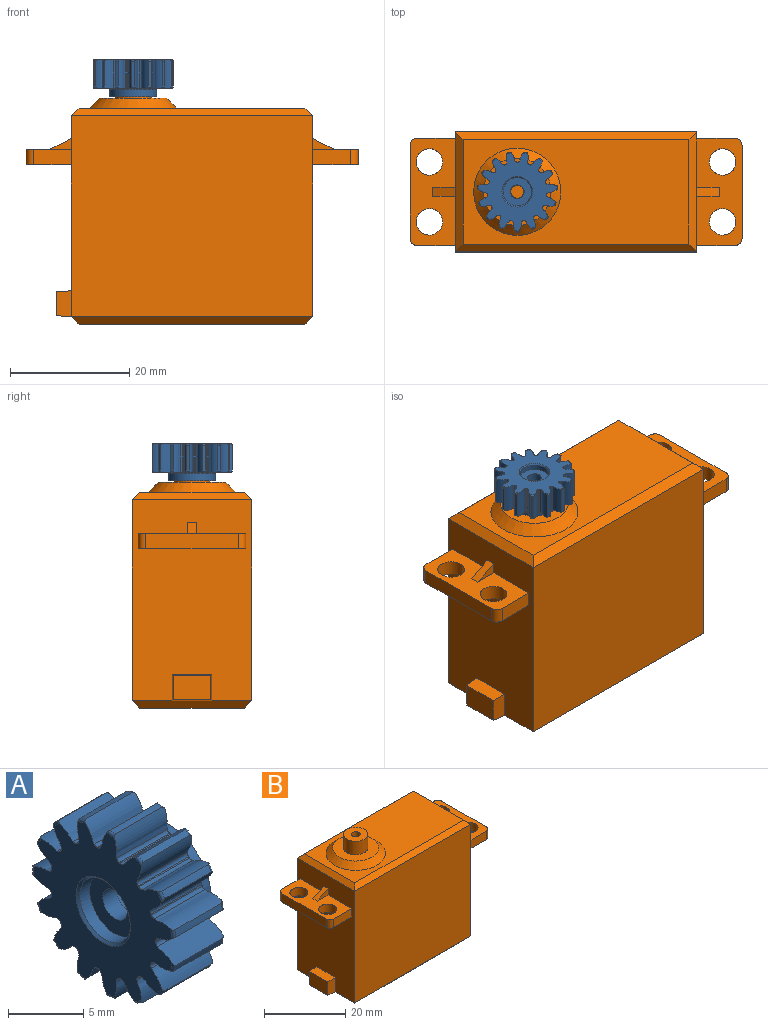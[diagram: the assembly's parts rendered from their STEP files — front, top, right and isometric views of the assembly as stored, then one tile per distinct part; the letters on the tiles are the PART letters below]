
ASSEMBLY  parts=2 mates=1
PART A: 131 faces, bbox 6.2x13.4x13.5 mm
  f0: cylinder r=2.38mm len=4.76mm, axis (-1,0,0), area 13.9mm2, adj f125,f130
  f1: cylinder r=3.96mm len=7.92mm, axis (1,0,0), area 31.3mm2, adj f124,f126
  f2: plane 13.08x13.02mm, normal (-1,0,0), area 86.7mm2, adj f3,f4,f5,f6,f7,f8,f9,f10
  f3: torus R=6.55mm, axis (-1,0,0), area 0.2mm2, adj f2,f18,f56,f57
  f4: torus R=6.55mm, axis (-1,0,0), area 0.2mm2, adj f2,f59,f60,f61
  f5: torus R=6.55mm, axis (-1,0,0), area 0.2mm2, adj f2,f64,f65,f66
  f6: torus R=6.55mm, axis (-1,0,0), area 0.2mm2, adj f2,f69,f70,f71
  f7: torus R=6.55mm, axis (-1,0,0), area 0.2mm2, adj f2,f74,f75,f76
  f8: torus R=6.55mm, axis (-1,0,0), area 0.2mm2, adj f2,f79,f80,f81
  f9: torus R=6.55mm, axis (-1,0,0), area 0.2mm2, adj f2,f84,f85,f86
  f10: torus R=6.55mm, axis (-1,0,0), area 0.2mm2, adj f2,f89,f90,f91
  f11: torus R=6.55mm, axis (-1,0,0), area 0.2mm2, adj f2,f36,f37,f38
  f12: torus R=6.55mm, axis (-1,0,0), area 0.2mm2, adj f2,f94,f95,f96
  f13: torus R=6.55mm, axis (-1,0,0), area 0.2mm2, adj f2,f99,f100,f101
  f14: torus R=6.55mm, axis (-1,0,0), area 0.2mm2, adj f2,f104,f105,f106
  f15: torus R=6.55mm, axis (-1,0,0), area 0.2mm2, adj f2,f109,f110,f111
  f16: torus R=6.55mm, axis (-1,0,0), area 0.2mm2, adj f2,f114,f115,f116
  f17: torus R=6.55mm, axis (-1,0,0), area 0.2mm2, adj f2,f119,f120,f121
  f18: extruded ~4.75x1.34mm, area 8.4mm2, adj f2,f3,f19,f40,f41,f57
  f19: cylinder r=0.31mm len=4.75mm, axis (1,0,0), area 1.6mm2, adj f2,f18,f34,f40
  f20: cylinder r=4.95mm len=4.75mm, axis (1,0,0), area 0.4mm2, adj f2,f35,f40,f92
  f21: cylinder r=4.95mm len=4.75mm, axis (1,0,0), area 0.4mm2, adj f2,f39,f40,f98
  f22: cylinder r=4.95mm len=4.75mm, axis (1,0,0), area 0.4mm2, adj f2,f40,f97,f103
  f23: cylinder r=4.95mm len=4.75mm, axis (1,0,0), area 0.4mm2, adj f2,f40,f102,f108
  f24: cylinder r=4.95mm len=4.75mm, axis (1,0,0), area 0.4mm2, adj f2,f40,f107,f113
  f25: cylinder r=4.95mm len=4.75mm, axis (1,0,0), area 0.4mm2, adj f2,f40,f112,f118
  f26: cylinder r=4.95mm len=4.75mm, axis (1,0,0), area 0.4mm2, adj f2,f40,f117,f123
  f27: cylinder r=4.95mm len=4.75mm, axis (1,0,0), area 0.4mm2, adj f2,f40,f88,f122
  f28: cylinder r=4.95mm len=4.75mm, axis (1,0,0), area 0.4mm2, adj f2,f40,f83,f87
  f29: cylinder r=4.95mm len=4.75mm, axis (1,0,0), area 0.4mm2, adj f2,f40,f78,f82
  f30: cylinder r=4.95mm len=4.75mm, axis (1,0,0), area 0.4mm2, adj f2,f40,f73,f77
  f31: cylinder r=4.95mm len=4.75mm, axis (1,0,0), area 0.4mm2, adj f2,f40,f68,f72
  f32: cylinder r=4.95mm len=4.75mm, axis (1,0,0), area 0.4mm2, adj f2,f40,f63,f67
  f33: cylinder r=4.95mm len=4.75mm, axis (1,0,0), area 0.4mm2, adj f2,f40,f58,f62
  f34: cylinder r=4.95mm len=4.75mm, axis (1,0,0), area 0.4mm2, adj f2,f19,f40,f93
  f35: cylinder r=0.31mm len=4.75mm, axis (1,0,0), area 1.6mm2, adj f2,f20,f36,f40
  f36: extruded ~4.75x1.34mm, area 8.4mm2, adj f2,f11,f35,f37,f40,f49
  f37: cylinder r=6.75mm len=4.35mm, axis (1,0,0), area 2.3mm2, adj f11,f36,f38,f49
  f38: extruded ~4.75x1.73mm, area 8.4mm2, adj f2,f11,f37,f39,f40,f49
  f39: cylinder r=0.31mm len=4.75mm, axis (1,0,0), area 1.6mm2, adj f2,f21,f38,f40
  f40: plane 13.08x13.02mm, normal (1,0,0), area 53.4mm2, adj f18,f19,f20,f21,f22,f23,f24,f25
  f41: torus R=6.55mm, axis (-1,0,0), area 0.2mm2, adj f18,f40,f56,f57
  f42: torus R=6.55mm, axis (-1,0,0), area 0.2mm2, adj f40,f59,f60,f61
  f43: torus R=6.55mm, axis (-1,0,0), area 0.2mm2, adj f40,f64,f65,f66
  f44: torus R=6.55mm, axis (-1,0,0), area 0.2mm2, adj f40,f69,f70,f71
  f45: torus R=6.55mm, axis (-1,0,0), area 0.2mm2, adj f40,f74,f75,f76
  f46: torus R=6.55mm, axis (-1,0,0), area 0.2mm2, adj f40,f79,f80,f81
  f47: torus R=6.55mm, axis (-1,0,0), area 0.2mm2, adj f40,f84,f85,f86
  f48: torus R=6.55mm, axis (-1,0,0), area 0.2mm2, adj f40,f89,f90,f91
  f49: torus R=6.55mm, axis (-1,0,0), area 0.2mm2, adj f36,f37,f38,f40
  f50: torus R=6.55mm, axis (-1,0,0), area 0.2mm2, adj f40,f94,f95,f96
  f51: torus R=6.55mm, axis (-1,0,0), area 0.2mm2, adj f40,f99,f100,f101
  f52: torus R=6.55mm, axis (-1,0,0), area 0.2mm2, adj f40,f104,f105,f106
  f53: torus R=6.55mm, axis (-1,0,0), area 0.2mm2, adj f40,f109,f110,f111
  f54: torus R=6.55mm, axis (-1,0,0), area 0.2mm2, adj f40,f114,f115,f116
  f55: torus R=6.55mm, axis (-1,0,0), area 0.2mm2, adj f40,f119,f120,f121
  f56: extruded ~4.75x1.73mm, area 8.4mm2, adj f2,f3,f40,f41,f57,f58
  f57: cylinder r=6.75mm len=4.35mm, axis (1,0,0), area 2.3mm2, adj f3,f18,f41,f56
  f58: cylinder r=0.31mm len=4.75mm, axis (1,0,0), area 1.6mm2, adj f2,f33,f40,f56
  f59: extruded ~4.75x1.49mm, area 8.4mm2, adj f2,f4,f40,f42,f60,f63
  f60: cylinder r=6.75mm len=4.35mm, axis (1,0,0), area 2.3mm2, adj f4,f42,f59,f61
  f61: extruded ~4.75x1.57mm, area 8.4mm2, adj f2,f4,f40,f42,f60,f62
  f62: cylinder r=0.31mm len=4.75mm, axis (1,0,0), area 1.6mm2, adj f2,f33,f40,f61
  f63: cylinder r=0.31mm len=4.75mm, axis (1,0,0), area 1.6mm2, adj f2,f32,f40,f59
  f64: extruded ~4.75x1.45mm, area 8.4mm2, adj f2,f5,f40,f43,f65,f68
  f65: cylinder r=6.75mm len=4.35mm, axis (1,0,0), area 2.3mm2, adj f5,f43,f64,f66
  f66: extruded ~4.75x1.75mm, area 8.4mm2, adj f2,f5,f40,f43,f65,f67
  f67: cylinder r=0.31mm len=4.75mm, axis (1,0,0), area 1.6mm2, adj f2,f32,f40,f66
  f68: cylinder r=0.31mm len=4.75mm, axis (1,0,0), area 1.6mm2, adj f2,f31,f40,f64
  f69: extruded ~4.75x1.72mm, area 8.4mm2, adj f2,f6,f40,f44,f70,f73
  f70: cylinder r=6.75mm len=4.35mm, axis (1,0,0), area 2.3mm2, adj f6,f44,f69,f71
  f71: extruded ~4.75x1.62mm, area 8.4mm2, adj f2,f6,f40,f44,f70,f72
  f72: cylinder r=0.31mm len=4.75mm, axis (1,0,0), area 1.6mm2, adj f2,f31,f40,f71
  f73: cylinder r=0.31mm len=4.75mm, axis (1,0,0), area 1.6mm2, adj f2,f30,f40,f69
  f74: extruded ~4.75x1.7mm, area 8.4mm2, adj f2,f7,f40,f45,f75,f78
  f75: cylinder r=6.75mm len=4.35mm, axis (1,0,0), area 2.3mm2, adj f7,f45,f74,f76
  f76: extruded ~4.75x1.26mm, area 8.4mm2, adj f2,f7,f40,f45,f75,f77
  f77: cylinder r=0.31mm len=4.75mm, axis (1,0,0), area 1.6mm2, adj f2,f30,f40,f76
  f78: cylinder r=0.31mm len=4.75mm, axis (1,0,0), area 1.6mm2, adj f2,f29,f40,f74
  f79: extruded ~4.75x1.38mm, area 8.4mm2, adj f2,f8,f40,f46,f80,f83
  f80: cylinder r=6.75mm len=4.35mm, axis (1,0,0), area 2.3mm2, adj f8,f46,f79,f81
  f81: extruded ~4.75x1.65mm, area 8.4mm2, adj f2,f8,f40,f46,f80,f82
  f82: cylinder r=0.31mm len=4.75mm, axis (1,0,0), area 1.6mm2, adj f2,f29,f40,f81
  f83: cylinder r=0.31mm len=4.75mm, axis (1,0,0), area 1.6mm2, adj f2,f28,f40,f79
  f84: extruded ~4.75x1.54mm, area 8.4mm2, adj f2,f9,f40,f47,f85,f88
  f85: cylinder r=6.75mm len=4.35mm, axis (1,0,0), area 2.3mm2, adj f9,f47,f84,f86
  f86: extruded ~4.75x1.74mm, area 8.4mm2, adj f2,f9,f40,f47,f85,f87
  f87: cylinder r=0.31mm len=4.75mm, axis (1,0,0), area 1.6mm2, adj f2,f28,f40,f86
  f88: cylinder r=0.31mm len=4.75mm, axis (1,0,0), area 1.6mm2, adj f2,f27,f40,f84
  f89: extruded ~4.75x1.68mm, area 8.4mm2, adj f2,f10,f40,f48,f90,f93
  f90: cylinder r=6.75mm len=4.35mm, axis (1,0,0), area 2.3mm2, adj f10,f48,f89,f91
  f91: extruded ~4.75x1.68mm, area 8.4mm2, adj f2,f10,f40,f48,f90,f92
  f92: cylinder r=0.31mm len=4.75mm, axis (1,0,0), area 1.6mm2, adj f2,f20,f40,f91
  f93: cylinder r=0.31mm len=4.75mm, axis (1,0,0), area 1.6mm2, adj f2,f34,f40,f89
  f94: extruded ~4.75x1.57mm, area 8.4mm2, adj f2,f12,f40,f50,f95,f98
  f95: cylinder r=6.75mm len=4.35mm, axis (1,0,0), area 2.3mm2, adj f12,f50,f94,f96
  f96: extruded ~4.75x1.49mm, area 8.4mm2, adj f2,f12,f40,f50,f95,f97
  f97: cylinder r=0.31mm len=4.75mm, axis (1,0,0), area 1.6mm2, adj f2,f22,f40,f96
  f98: cylinder r=0.31mm len=4.75mm, axis (1,0,0), area 1.6mm2, adj f2,f21,f40,f94
  f99: extruded ~4.75x1.75mm, area 8.4mm2, adj f2,f13,f40,f51,f100,f103
  f100: cylinder r=6.75mm len=4.35mm, axis (1,0,0), area 2.3mm2, adj f13,f51,f99,f101
  f101: extruded ~4.75x1.45mm, area 8.4mm2, adj f2,f13,f40,f51,f100,f102
  f102: cylinder r=0.31mm len=4.75mm, axis (1,0,0), area 1.6mm2, adj f2,f23,f40,f101
  f103: cylinder r=0.31mm len=4.75mm, axis (1,0,0), area 1.6mm2, adj f2,f22,f40,f99
  f104: extruded ~4.75x1.62mm, area 8.4mm2, adj f2,f14,f40,f52,f105,f108
  f105: cylinder r=6.75mm len=4.35mm, axis (1,0,0), area 2.3mm2, adj f14,f52,f104,f106
  f106: extruded ~4.75x1.72mm, area 8.4mm2, adj f2,f14,f40,f52,f105,f107
  f107: cylinder r=0.31mm len=4.75mm, axis (1,0,0), area 1.6mm2, adj f2,f24,f40,f106
  f108: cylinder r=0.31mm len=4.75mm, axis (1,0,0), area 1.6mm2, adj f2,f23,f40,f104
  f109: extruded ~4.75x1.26mm, area 8.4mm2, adj f2,f15,f40,f53,f110,f113
  f110: cylinder r=6.75mm len=4.35mm, axis (1,0,0), area 2.3mm2, adj f15,f53,f109,f111
  f111: extruded ~4.75x1.7mm, area 8.4mm2, adj f2,f15,f40,f53,f110,f112
  f112: cylinder r=0.31mm len=4.75mm, axis (1,0,0), area 1.6mm2, adj f2,f25,f40,f111
  f113: cylinder r=0.31mm len=4.75mm, axis (1,0,0), area 1.6mm2, adj f2,f24,f40,f109
  f114: extruded ~4.75x1.65mm, area 8.4mm2, adj f2,f16,f40,f54,f115,f118
  f115: cylinder r=6.75mm len=4.35mm, axis (1,0,0), area 2.3mm2, adj f16,f54,f114,f116
  f116: extruded ~4.75x1.38mm, area 8.4mm2, adj f2,f16,f40,f54,f115,f117
  f117: cylinder r=0.31mm len=4.75mm, axis (1,0,0), area 1.6mm2, adj f2,f26,f40,f116
  f118: cylinder r=0.31mm len=4.75mm, axis (1,0,0), area 1.6mm2, adj f2,f25,f40,f114
  f119: extruded ~4.75x1.74mm, area 8.4mm2, adj f2,f17,f40,f55,f120,f123
  f120: cylinder r=6.75mm len=4.35mm, axis (1,0,0), area 2.3mm2, adj f17,f55,f119,f121
  f121: extruded ~4.75x1.54mm, area 8.4mm2, adj f2,f17,f40,f55,f120,f122
  f122: cylinder r=0.31mm len=4.75mm, axis (1,0,0), area 1.6mm2, adj f2,f27,f40,f121
  f123: cylinder r=0.31mm len=4.75mm, axis (1,0,0), area 1.6mm2, adj f2,f26,f40,f119
  f124: torus R=4.14mm, axis (1,0,0), area 7.1mm2, adj f1,f40
  f125: cone r=2.47mm half-angle=45deg, axis (-1,0,0), area 3.9mm2, adj f0,f2
  f126: plane 7.92x7.92mm, normal (1,0,0), area 20.1mm2, adj f1,f127
  f127: cylinder r=3.05mm len=6.1mm, axis (1,0,0), area 73mm2, adj f126,f128
  f128: plane 6.1x6.1mm, normal (1,0,0), area 25.1mm2, adj f127,f129
  f129: cylinder r=1.14mm len=2.29mm, axis (1,0,0), area 9.1mm2, adj f128,f130
  f130: plane 4.76x4.76mm, normal (-1,0,0), area 13.7mm2, adj f0,f129
PART B: 49 faces, bbox 55.6x20.1x41.9 mm
  f0: plane 33.66x20.07mm, normal (-1,0,0), area 598.1mm2, adj f1,f3,f6,f7,f8,f9,f11,f12
  f1: plane 40.39x33.66mm, normal (0,-1,0), area 1359.2mm2, adj f0,f2,f35,f39
  f2: plane 33.66x20.07mm, normal (1,0,0), area 626.6mm2, adj f1,f3,f18,f19,f20,f21,f23,f24
  f3: plane 40.39x33.66mm, normal (0,1,0), area 1359.2mm2, adj f0,f2,f36,f40
  f4: plane 37.85x17.53mm, normal (0,0,1), area 495.8mm2, adj f33,f38,f39,f40,f41
  f5: plane 37.85x17.53mm, normal (0,0,-1), area 663.3mm2, adj f34,f35,f36,f37
  f6: plane 18.03x7.62mm, normal (0,0,1), area 99.9mm2, adj f0,f8,f9,f10,f11,f12,f13,f14
  f7: plane 18.03x7.62mm, normal (0,0,-1), area 105.7mm2, adj f0,f8,f9,f10,f14,f15,f16,f17
  f8: plane 6.35x2.54mm, normal (0,1,0), area 16.1mm2, adj f0,f6,f7,f16
  f9: plane 6.35x2.54mm, normal (0,-1,0), area 16.1mm2, adj f0,f6,f7,f17
  f10: plane 15.49x2.54mm, normal (-1,0,0), area 39.4mm2, adj f6,f7,f16,f17
  f11: plane 3.81x1.91mm, normal (0,-1,0), area 3.6mm2, adj f0,f6,f13
  f12: plane 3.81x1.91mm, normal (0,1,0), area 3.6mm2, adj f0,f6,f13
  f13: plane 3.81x1.91mm, normal (-0.45,0,0.89), area 6.5mm2, adj f0,f6,f11,f12
  f14: cylinder r=2.22mm len=4.45mm, axis (0,0,1), area 35.5mm2, adj f6,f7
  f15: cylinder r=2.22mm len=4.45mm, axis (0,0,1), area 35.5mm2, adj f6,f7
  f16: cylinder r=1.27mm len=2.54mm, axis (0,0,1), area 5.1mm2, adj f6,f7,f8,f10
  f17: cylinder r=1.27mm len=2.54mm, axis (0,0,-1), area 5.1mm2, adj f6,f7,f9,f10
  f18: plane 18.03x7.62mm, normal (0,0,1), area 99.9mm2, adj f2,f20,f21,f22,f23,f24,f25,f26
  f19: plane 18.03x7.62mm, normal (0,0,-1), area 105.7mm2, adj f2,f20,f21,f22,f26,f27,f28,f29
  f20: plane 6.35x2.54mm, normal (0,1,0), area 16.1mm2, adj f2,f18,f19,f28
  f21: plane 6.35x2.54mm, normal (0,-1,0), area 16.1mm2, adj f2,f18,f19,f29
  f22: plane 15.49x2.54mm, normal (1,0,0), area 39.4mm2, adj f18,f19,f28,f29
  f23: plane 3.81x1.91mm, normal (0,-1,0), area 3.6mm2, adj f2,f18,f25
  f24: plane 3.81x1.91mm, normal (0,1,0), area 3.6mm2, adj f2,f18,f25
  f25: plane 3.81x1.91mm, normal (0.45,0,0.89), area 6.5mm2, adj f2,f18,f23,f24
  f26: cylinder r=2.22mm len=4.45mm, axis (0,0,1), area 35.5mm2, adj f18,f19
  f27: cylinder r=2.22mm len=4.45mm, axis (0,0,1), area 35.5mm2, adj f18,f19
  f28: cylinder r=1.27mm len=2.54mm, axis (0,0,1), area 5.1mm2, adj f18,f19,f20,f22
  f29: cylinder r=1.27mm len=2.54mm, axis (0,0,-1), area 5.1mm2, adj f18,f19,f21,f22
  f30: plane 11.3x11.3mm, normal (0,0,1), area 72.4mm2, adj f31,f33
  f31: cylinder r=2.98mm len=5.97mm, axis (0,0,-1), area 76.2mm2, adj f30,f32
  f32: plane 5.97x5.97mm, normal (0,0,1), area 24.3mm2, adj f31,f47
  f33: cone r=5.65mm half-angle=45deg, axis (0,0,-1), area 95mm2, adj f4,f30
  f34: plane 20.07x1.27mm, normal (0.71,0,-0.71), area 33.8mm2, adj f2,f5,f35,f36
  f35: plane 40.39x1.27mm, normal (0,-0.71,-0.71), area 70.3mm2, adj f1,f5,f34,f37
  f36: plane 40.39x1.27mm, normal (0,0.71,-0.71), area 70.3mm2, adj f3,f5,f34,f37
  f37: plane 20.07x1.27mm, normal (-0.71,0,-0.71), area 33.8mm2, adj f0,f5,f35,f36,f42
  f38: plane 20.07x1.27mm, normal (0.71,0,0.71), area 33.8mm2, adj f2,f4,f39,f40
  f39: plane 40.39x1.27mm, normal (0,-0.71,0.71), area 70.3mm2, adj f1,f4,f38,f41
  f40: plane 40.39x1.27mm, normal (0,0.71,0.71), area 70.3mm2, adj f3,f4,f38,f41
  f41: plane 20.07x1.27mm, normal (-0.71,0,0.71), area 33.8mm2, adj f0,f4,f39,f40
  f42: plane 6.6x2.54mm, normal (-0.05,0,-1), area 16.5mm2, adj f37,f43,f45,f46
  f43: plane 4.32x2.54mm, normal (-0.05,-1,0), area 10.6mm2, adj f0,f42,f44,f46
  f44: plane 6.6x2.54mm, normal (-0.05,0,1), area 16.5mm2, adj f0,f43,f45,f46
  f45: plane 4.32x2.54mm, normal (-0.05,1,0), area 10.6mm2, adj f0,f42,f44,f46
  f46: plane 6.34x4.05mm, normal (-1,0,0), area 25.7mm2, adj f42,f43,f44,f45
  f47: cylinder r=1.08mm len=2.54mm, axis (0,0,1), area 17.2mm2, adj f32,f48
  f48: plane 2.16x2.16mm, normal (0,0,1), area 3.7mm2, adj f47
PLACE A rot(axis=(0.71,0,-0.71),180deg) t=(-8.51,4.18,26.07)mm
PLACE B t=(1.33,4.18,-15.84)mm
MATE revolute A.f129 <-> B.f47  axis (0,0,-1) through (-8.51,4.18,26.07)mm
